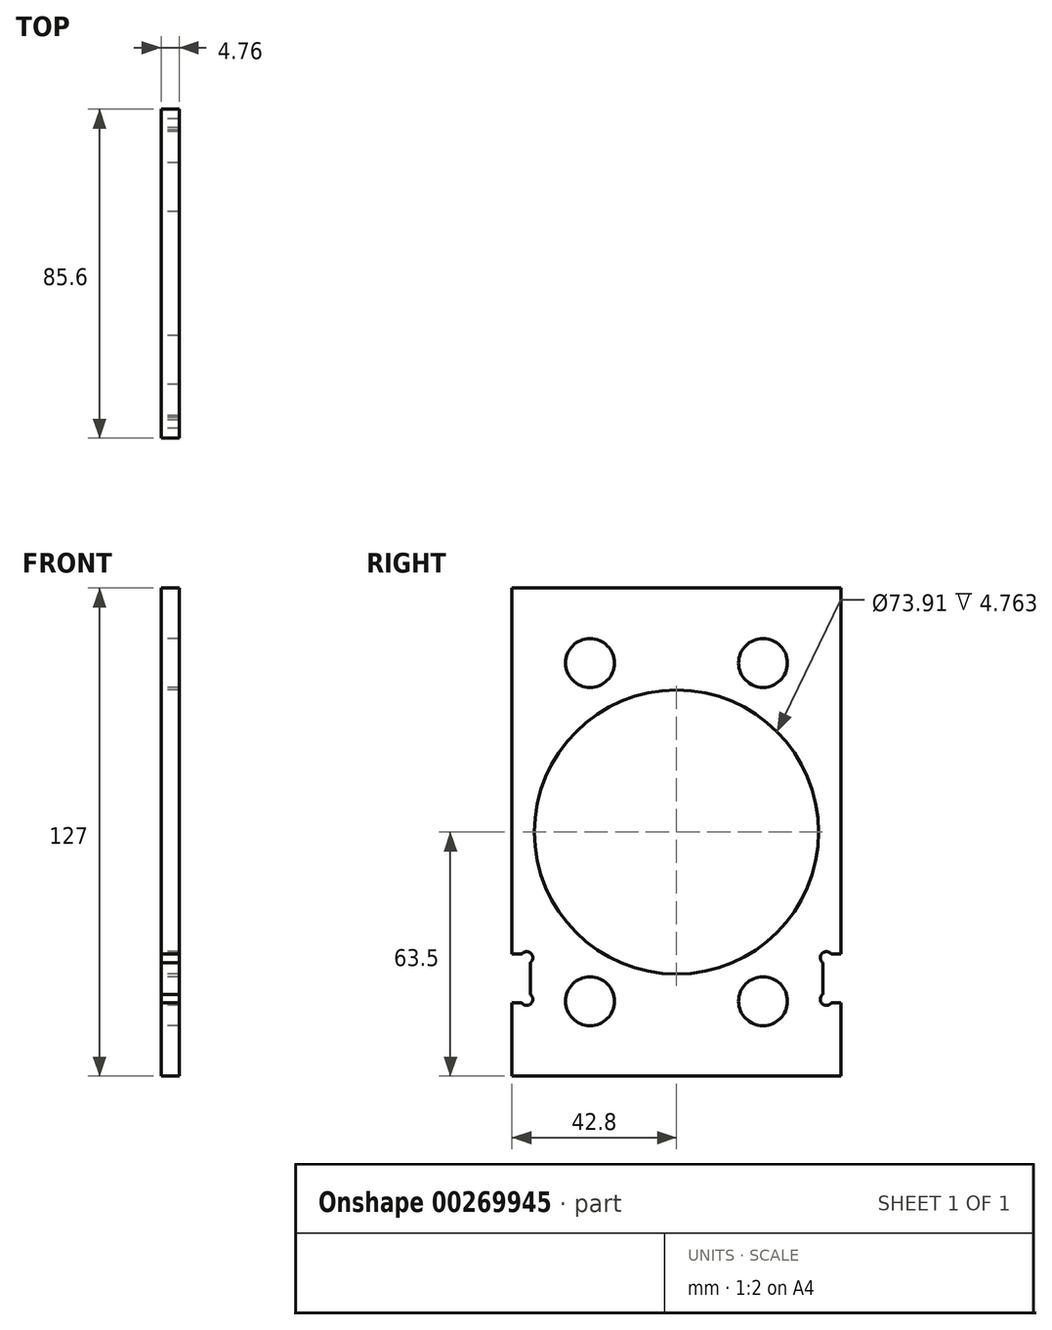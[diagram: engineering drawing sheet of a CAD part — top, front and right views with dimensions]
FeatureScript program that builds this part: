
annotation { "Feature Type Name" : "Feature", "Feature Type Description" : "" }
export const myFeature = defineFeature(function(context is Context, id is Id, definition is map)
    precondition{}
    {
        {
            var Q0;
            Q0=qCreatedBy(makeId("Right.planeOp"),FACE);
            var sketch = newSketch(context, id + "F0", { "sketchPlane" : qUnion([Q0])});
            skCircle(sketch, "E0", {"center": v(0, 0) * mm, "radius": 36.96 * mm});
            skCircle(sketch, "E1", {"center": v(-22.5, 44) * mm, "radius": 6.35 * mm});
            skCircle(sketch, "E2", {"center": v(22.5, 44) * mm, "radius": 6.35 * mm});
            skCircle(sketch, "E3", {"center": v(22.5, -44) * mm, "radius": 6.35 * mm});
            skCircle(sketch, "E4", {"center": v(-22.5, -44) * mm, "radius": 6.35 * mm});
            skLineSegment(sketch, "E5.bottom", {"start": v(-42.8, 63.5) * mm, "end": v(42.8, 63.5) * mm});
            skLineSegment(sketch, "E5.top", {"start": v(-42.8, -63.5) * mm, "end": v(42.8, -63.5) * mm});
            skLineSegment(sketch, "E5.left", {"start": v(-42.8, 63.5) * mm, "end": v(-42.8, -63.5) * mm});
            skLineSegment(sketch, "E5.right", {"start": v(42.8, 63.5) * mm, "end": v(42.8, -63.5) * mm});
            skSolve(sketch);
        }
        {
            var Q0;
            Q0=makeQuery(id+"F0.imprint","IMPRINT",FACE,{"disambiguationData":[TD([[makeQuery(id+"F0.imprint","IMPRINT",EDGE,{"derivedFrom":sQuery(id+"F0.wireOp",EDGE,"E0")}),-1.0]])]});
            extrude(context, id + "F1", {"entities" : qUnion([Q0]), "depth" : 4.76 * mm});
        }
        {
            var Q0;
            Q0=qCreatedBy(makeId("Right.planeOp"),FACE);
            var sketch = newSketch(context, id + "F2", { "sketchPlane" : qUnion([Q0])});
            skLineSegment(sketch, "E6.bottom", {"start": v(-42.8, -44.45) * mm, "end": v(-40.26, -44.45) * mm});
            skLineSegment(sketch, "E6.top", {"start": v(-42.8, -31.75) * mm, "end": v(-40.26, -31.75) * mm});
            skLineSegment(sketch, "E6.left", {"start": v(-42.8, -44.45) * mm, "end": v(-42.8, -31.75) * mm});
            skLineSegment(sketch, "E6.right", {"start": v(-38.04, -42.23) * mm, "end": v(-38.04, -33.97) * mm});
            skLineSegment(sketch, "E7", {"start": v(-38.04, -44.45) * mm, "end": v(-44.62, -37.86) * mm, "construction": true});
            skLineSegment(sketch, "E8", {"start": v(-38.04, -31.75) * mm, "end": v(-46.55, -40.27) * mm, "construction": true});
            skArc(sketch, "E9", {"start": v(-40.26, -44.45) * mm, "mid": v(-37.86, -44.63) * mm, "end": v(-38.04, -42.23) * mm});
            skArc(sketch, "E10", {"start": v(-38.04, -33.97) * mm, "mid": v(-37.86, -31.57) * mm, "end": v(-40.26, -31.75) * mm});
            skLineSegment(sketch, "E11.MirrorCS", {"start": v(42.8, -31.75) * mm, "end": v(40.26, -31.75) * mm});
            skLineSegment(sketch, "E12.MirrorCS", {"start": v(42.8, -44.45) * mm, "end": v(40.26, -44.45) * mm});
            skArc(sketch, "E13.MirrorCS", {"start": v(40.26, -44.45) * mm, "mid": v(37.86, -44.63) * mm, "end": v(38.04, -42.23) * mm});
            skArc(sketch, "E14.MirrorCS", {"start": v(38.04, -33.97) * mm, "mid": v(37.86, -31.57) * mm, "end": v(40.26, -31.75) * mm});
            skLineSegment(sketch, "E15.MirrorCS", {"start": v(38.04, -42.23) * mm, "end": v(38.04, -33.97) * mm});
            skLineSegment(sketch, "E16.MirrorCS", {"start": v(38.04, -31.75) * mm, "end": v(46.55, -40.27) * mm, "construction": true});
            skLineSegment(sketch, "E17.MirrorCS", {"start": v(38.04, -44.45) * mm, "end": v(44.62, -37.86) * mm, "construction": true});
            skLineSegment(sketch, "E18.MirrorCS", {"start": v(42.8, -44.45) * mm, "end": v(42.8, -31.75) * mm});
            skSolve(sketch);
        }
        {
            var Q0;
            Q0 = qSketchRegion(id + "F2", true);
            extrude(context, id + "F3", {"entities" : qUnion([Q0]), "operationType" : NewBodyOperationType.REMOVE, "endBound" : BoundingType.THROUGH_ALL, "depth" : 25.4 * mm});
        }
    });
